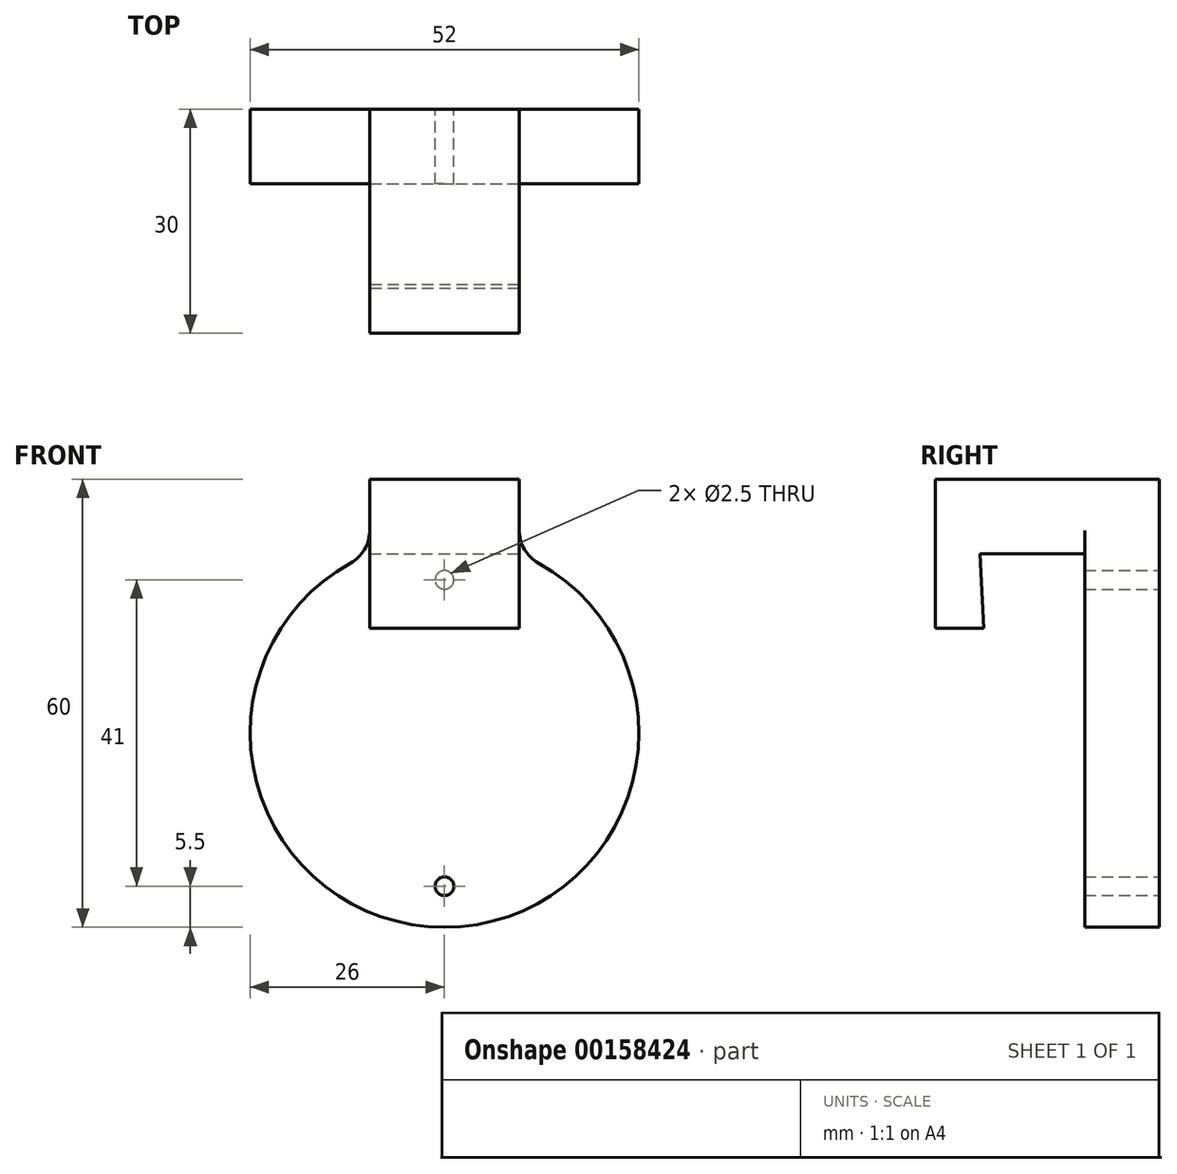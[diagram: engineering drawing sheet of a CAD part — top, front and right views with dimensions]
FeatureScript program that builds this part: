
annotation { "Feature Type Name" : "Feature", "Feature Type Description" : "" }
export const myFeature = defineFeature(function(context is Context, id is Id, definition is map)
    precondition{}
    {
        {
            var Q0;
            Q0=qCreatedBy(makeId("Front.planeOp"),FACE);
            var sketch = newSketch(context, id + "F0", { "sketchPlane" : qUnion([Q0])});
            skArc(sketch, "E0", {"start": v(-10, 24) * mm, "mid": v(0, -26) * mm, "end": v(10, 24) * mm});
            skPoint(sketch, "E1", {"position": v(0, 20.5) * mm});
            skPoint(sketch, "E2.MirrorP", {"position": v(0, -20.5) * mm});
            skLineSegment(sketch, "E3", {"start": v(-10, 24) * mm, "end": v(-10, 34) * mm});
            skLineSegment(sketch, "E4", {"start": v(-10, 34) * mm, "end": v(10, 34) * mm});
            skLineSegment(sketch, "E5", {"start": v(10, 34) * mm, "end": v(10, 24) * mm});
            skSolve(sketch);
        }
        {
            var Q0;
            Q0=makeQuery(id+"F0.imprint","IMPRINT",FACE,{"disambiguationData":[TD([[makeQuery(id+"F0.imprint","IMPRINT",EDGE,{"derivedFrom":sQuery(id+"F0.wireOp",EDGE,"E0")}),1.0]])]});
            extrude(context, id + "F1", {"entities" : qUnion([Q0]), "depth" : 10 * mm});
        }
        {
            var Q0;
            Q0=sQuery(id+"F0.wireOp",VERTEX,"E2.MirrorP");
            var Q1;
            Q1=sQuery(id+"F0.wireOp",VERTEX,"E1");
            var Q2;
            Q2=makeQuery(id+"F1.opExtrude","SWEPT_BODY",BODY,{"disambiguationData":[OSD([sQuery(id+"F0.wireOp",EDGE,"E0"),sQuery(id+"F0.wireOp",EDGE,"E3"),sQuery(id+"F0.wireOp",EDGE,"E4"),sQuery(id+"F0.wireOp",EDGE,"E5")])]});
            hole(context, id + "F2", {"style" : HoleStyle.SIMPLE, "endStyle" : HoleEndStyle.THROUGH, "oppositeDirection" : true, "holeDiameter" : 2.5 * mm, "locations" : qUnion([Q0, Q1]), "scope" : qUnion([Q2]), "isTappedThrough" : true});
        }
        {
            var Q0;
            Q0=makeQuery(id+"F1.opExtrude","CAP_FACE",FACE,{"disambiguationData":[OSD([sQuery(id+"F0.wireOp",EDGE,"E0"),sQuery(id+"F0.wireOp",EDGE,"E3"),sQuery(id+"F0.wireOp",EDGE,"E4"),sQuery(id+"F0.wireOp",EDGE,"E5")])],"isStart":false});
            var sketch = newSketch(context, id + "F3", { "sketchPlane" : qUnion([Q0])});
            skLineSegment(sketch, "E6", {"start": v(-10, 24) * mm, "end": v(10, 24) * mm});
            skSolve(sketch);
        }
        {
            var Q0;
            Q0 = qSketchRegion(id + "F3", true);
            var Q1;
            Q1=makeQuery(id+"F3.imprint","IMPRINT",FACE,{"disambiguationData":[TD([[makeQuery(id+"F3.imprint","IMPRINT",EDGE,{"derivedFrom":sQuery(id+"F3.wireOp",EDGE,"E6")}),1.0]])]});
            extrude(context, id + "F4", {"entities" : qUnion([Q0, Q1]), "operationType" : NewBodyOperationType.ADD, "depth" : 20 * mm});
        }
        {
            var Q0;
            {var subQ0=sQuery(id+"F0.wireOp",EDGE,"E3");Q0=makeQuery(id+"F4.boolean.opBoolean","MERGE",FACE,{"derivedFrom":[makeQuery(id+"F1.opExtrude","SWEPT_FACE",FACE,{"disambiguationData":[OSD([subQ0])]}),makeQuery(id+"F4.opExtrude","SWEPT_FACE",FACE,{"disambiguationData":[OSD([subQ0])]})]});}
            var sketch = newSketch(context, id + "F5", { "sketchPlane" : qUnion([Q0])});
            skLineSegment(sketch, "E7", {"start": v(30, 24) * mm, "end": v(30, 14) * mm});
            skLineSegment(sketch, "E8", {"start": v(30, 14) * mm, "end": v(23.5, 14) * mm});
            skLineSegment(sketch, "E9", {"start": v(23.5, 14) * mm, "end": v(24, 24) * mm});
            skSolve(sketch);
        }
        {
            var Q0;
            {var subQ0=sQuery(id+"F5.wireOp",EDGE,"E7");Q0=makeQuery(id+"F5.imprint","IMPRINT",FACE,{"disambiguationData":[TD([[makeQuery(id+"F5.imprint","IMPRINT",EDGE,{"derivedFrom":subQ0}),-1.0]])]});}
            var Q1;
            {var subQ0=sQuery(id+"F0.wireOp",EDGE,"E5");Q1=makeQuery(id+"F4.boolean.opBoolean","MERGE",FACE,{"derivedFrom":[makeQuery(id+"F1.opExtrude","SWEPT_FACE",FACE,{"disambiguationData":[OSD([subQ0])]}),makeQuery(id+"F4.opExtrude","SWEPT_FACE",FACE,{"disambiguationData":[OSD([subQ0])]})]});}
            extrude(context, id + "F6", {"entities" : qUnion([Q0]), "operationType" : NewBodyOperationType.ADD, "endBound" : BoundingType.UP_TO_SURFACE, "oppositeDirection" : true, "endBoundEntityFace" : qUnion([Q1]), "depth" : 25 * mm});
        }
        {
            var Q0;
            Q0=makeQuery(id+"F1.opExtrude","SWEPT_EDGE",EDGE,{"disambiguationData":[OSD([sQuery(id+"F0.wireOp",EDGE,"E0"),sQuery(id+"F0.wireOp",EDGE,"E5")])]});
            var Q1;
            Q1=makeQuery(id+"F1.opExtrude","SWEPT_EDGE",EDGE,{"disambiguationData":[OSD([sQuery(id+"F0.wireOp",EDGE,"E0"),sQuery(id+"F0.wireOp",EDGE,"E3")])]});
            fillet(context, id + "F7", {"entities" : qUnion([Q0, Q1]), "radius" : 5 * mm, "tangentPropagation" : true, "allowEdgeOverflow" : false});
        }
    });
